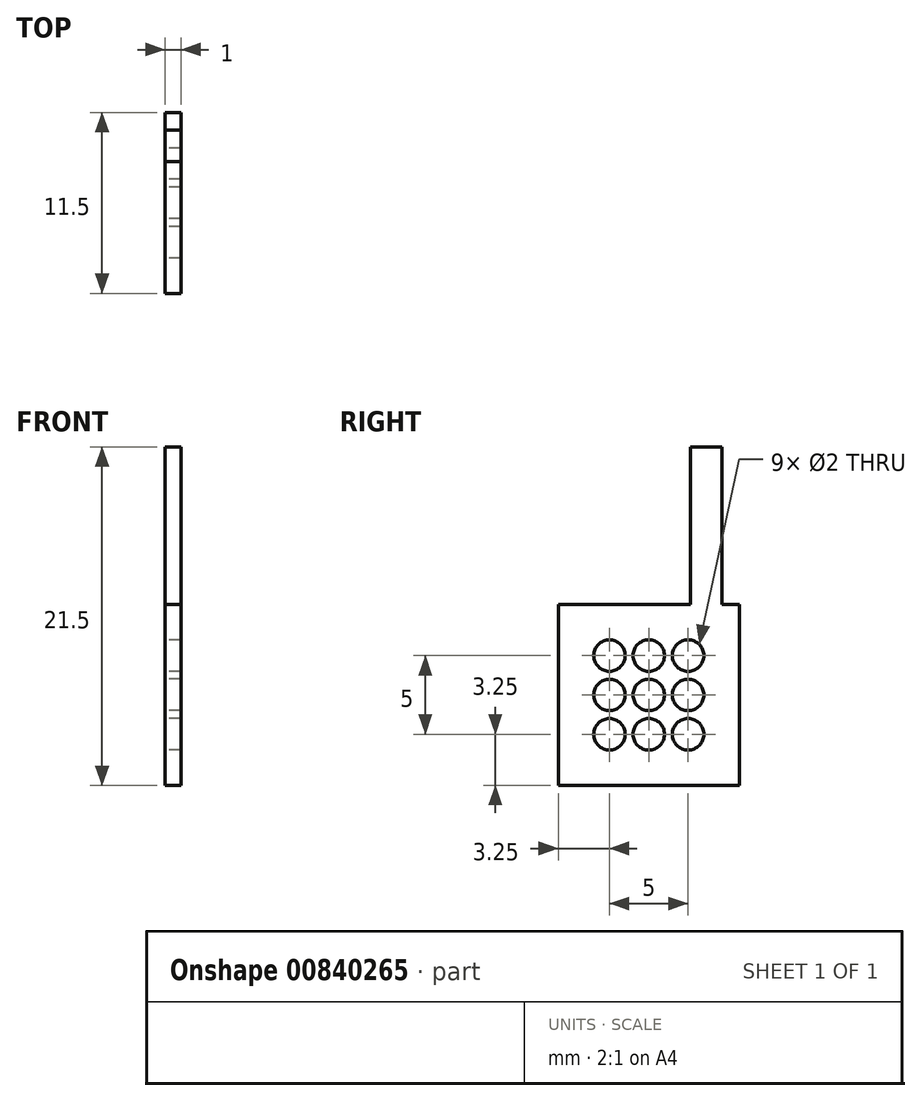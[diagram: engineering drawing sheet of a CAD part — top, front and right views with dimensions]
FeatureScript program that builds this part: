
annotation { "Feature Type Name" : "Feature", "Feature Type Description" : "" }
export const myFeature = defineFeature(function(context is Context, id is Id, definition is map)
    precondition{}
    {
        {
            var Q0;
            Q0=qCreatedBy(makeId("Right.planeOp"),FACE);
            var sketch = newSketch(context, id + "F0", { "sketchPlane" : qUnion([Q0])});
            skLineSegment(sketch, "E0.bottom", {"start": v(0, 0) * mm, "end": v(8.38, 0) * mm});
            skLineSegment(sketch, "E0.top", {"start": v(0, -11.5) * mm, "end": v(11.5, -11.5) * mm});
            skLineSegment(sketch, "E0.left", {"start": v(0, 0) * mm, "end": v(0, -11.5) * mm});
            skCircle(sketch, "E1", {"center": v(5.75, -5.75) * mm, "radius": 1 * mm});
            skLineSegment(sketch, "E2", {"start": v(11.5, 0) * mm, "end": v(11.5, -11.5) * mm});
            skLineSegment(sketch, "E3", {"start": v(10.38, 0) * mm, "end": v(10.38, 10) * mm});
            skLineSegment(sketch, "E4", {"start": v(10.38, 10) * mm, "end": v(8.38, 10) * mm});
            skLineSegment(sketch, "E5", {"start": v(8.38, 10) * mm, "end": v(8.38, 0) * mm});
            skLineSegment(sketch, "E6.trimOffspring", {"start": v(10.38, 0) * mm, "end": v(11.5, 0) * mm});
            skCircle(sketch, "E7", {"center": v(5.75, -3.25) * mm, "radius": 1 * mm});
            skCircle(sketch, "E8", {"center": v(3.25, -5.75) * mm, "radius": 1 * mm});
            skCircle(sketch, "E9", {"center": v(3.25, -3.25) * mm, "radius": 1 * mm});
            skCircle(sketch, "E10.MirrorC", {"center": v(8.25, -3.25) * mm, "radius": 1 * mm});
            skCircle(sketch, "E11.MirrorC", {"center": v(8.25, -5.75) * mm, "radius": 1 * mm});
            skCircle(sketch, "E12.MirrorC", {"center": v(3.25, -8.25) * mm, "radius": 1 * mm});
            skCircle(sketch, "E13.MirrorC", {"center": v(8.25, -8.25) * mm, "radius": 1 * mm});
            skCircle(sketch, "E14.MirrorC", {"center": v(5.75, -8.25) * mm, "radius": 1 * mm});
            skSolve(sketch);
        }
        {
            var Q0;
            Q0=makeQuery(id+"F0.imprint","IMPRINT",FACE,{"disambiguationData":[TD([[makeQuery(id+"F0.imprint","IMPRINT",EDGE,{"derivedFrom":sQuery(id+"F0.wireOp",EDGE,"E0.bottom")}),-1.0]])]});
            var Q1;
            Q1=makeQuery(id+"F0.imprint","IMPRINT",FACE,{"disambiguationData":[TD([[makeQuery(id+"F0.imprint","IMPRINT",EDGE,{"derivedFrom":sQuery(id+"F0.wireOp",EDGE,"r65wuaeR-pUGk-UfhY-v5oq-7bkjaNJfQmKm.bottom")}),-1.0]])]});
            var Q2;
            Q2=makeQuery(id+"F0.imprint","IMPRINT",FACE,{"disambiguationData":[TD([[makeQuery(id+"F0.imprint","IMPRINT",EDGE,{"derivedFrom":sQuery(id+"F0.wireOp",EDGE,"n5EaUuf3-CoM6-EQkv-XzT1-ydr3onYee1LO.bottom")}),1.0]])]});
            var Q3;
            Q3=makeQuery(id+"F0.imprint","IMPRINT",FACE,{"disambiguationData":[TD([[makeQuery(id+"F0.imprint","IMPRINT",EDGE,{"derivedFrom":sQuery(id+"F0.wireOp",EDGE,"2NUbogVr-x7fL-9LVX-WR3f-6RiyyzUn8nbi.bottom")}),-1.0]])]});
            extrude(context, id + "F1", {"entities" : qUnion([Q0, Q1, Q2, Q3]), "depth" : 1 * mm, "offsetDistance" : 25 * mm});
        }
    });
